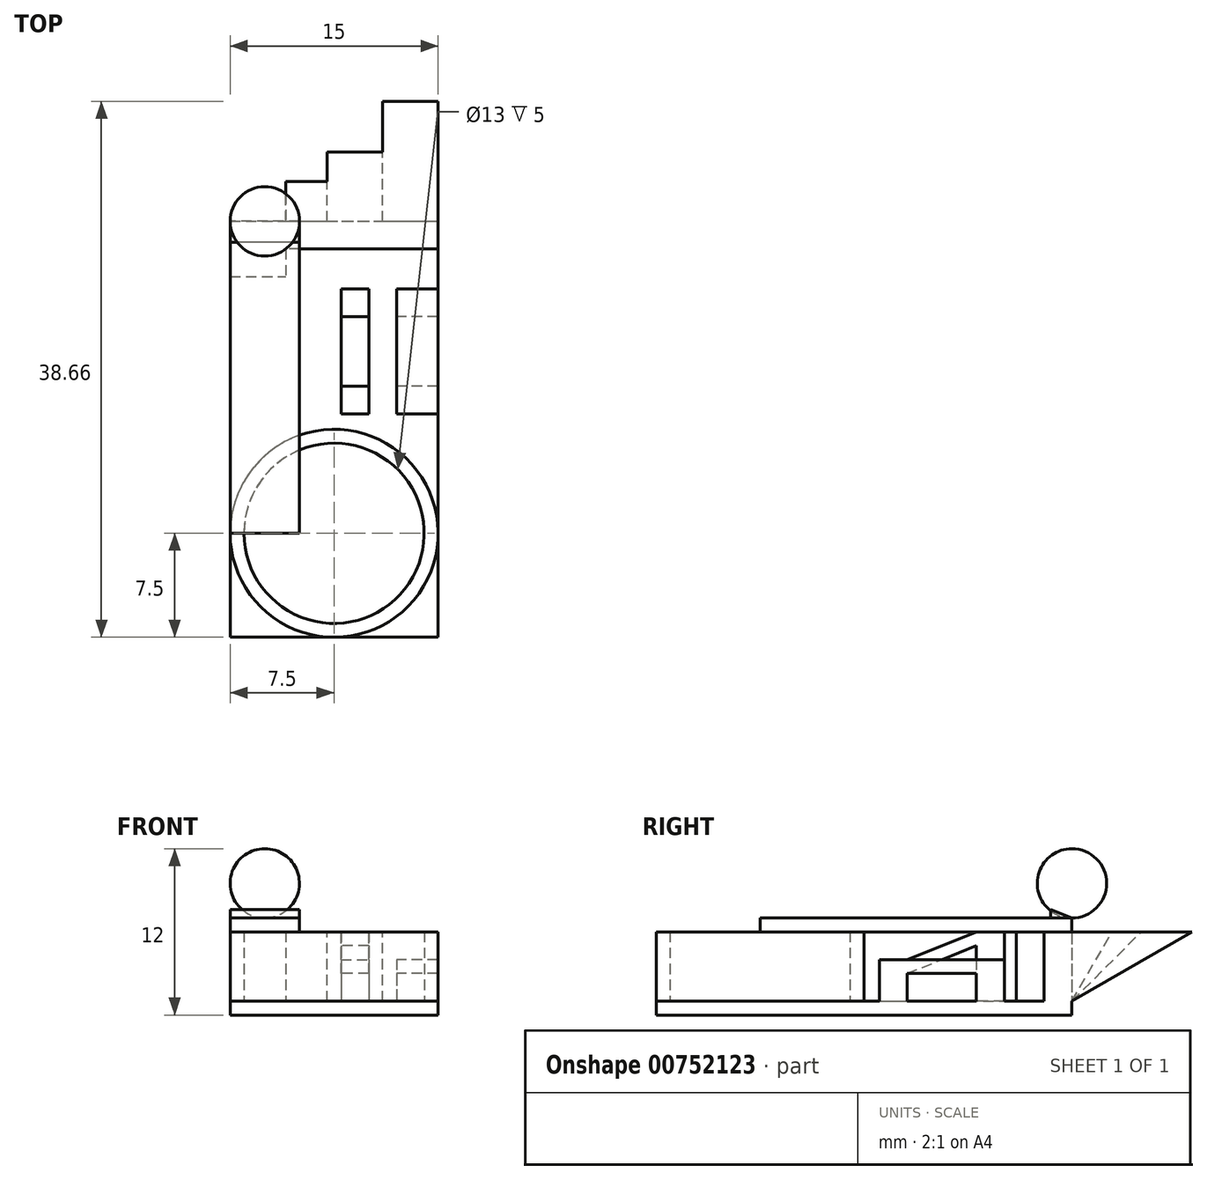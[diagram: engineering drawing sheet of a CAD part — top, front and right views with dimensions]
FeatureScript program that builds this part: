
annotation { "Feature Type Name" : "Feature", "Feature Type Description" : "" }
export const myFeature = defineFeature(function(context is Context, id is Id, definition is map)
    precondition{}
    {
        {
            var Q0;
            Q0=qCreatedBy(makeId("Top.planeOp"),FACE);
            var sketch = newSketch(context, id + "F0", { "sketchPlane" : qUnion([Q0])});
            skLineSegment(sketch, "E0.bottom", {"start": v(0, 0) * mm, "end": v(15, 0) * mm});
            skLineSegment(sketch, "E0.top", {"start": v(0, 30) * mm, "end": v(15, 30) * mm});
            skLineSegment(sketch, "E0.left", {"start": v(0, 0) * mm, "end": v(0, 30) * mm});
            skLineSegment(sketch, "E0.right", {"start": v(15, 0) * mm, "end": v(15, 30) * mm});
            skSolve(sketch);
        }
        {
            var Q0;
            Q0=makeQuery(id+"F0.imprint","IMPRINT",FACE,{"disambiguationData":[TD([[makeQuery(id+"F0.imprint","IMPRINT",EDGE,{"derivedFrom":sQuery(id+"F0.wireOp",EDGE,"E0.bottom")}),1.0]])]});
            extrude(context, id + "F1", {"entities" : qUnion([Q0]), "depth" : 1 * mm, "offsetDistance" : 25 * mm});
        }
        {
            var Q0;
            Q0=makeQuery(id+"F1.opExtrude","CAP_FACE",FACE,{"disambiguationData":[OSD([sQuery(id+"F0.wireOp",EDGE,"E0.bottom"),sQuery(id+"F0.wireOp",EDGE,"E0.top"),sQuery(id+"F0.wireOp",EDGE,"E0.left"),sQuery(id+"F0.wireOp",EDGE,"E0.right")])],"isStart":false});
            var sketch = newSketch(context, id + "F2", { "sketchPlane" : qUnion([Q0])});
            skCircle(sketch, "E1", {"center": v(7.5, 7.5) * mm, "radius": 7.5 * mm});
            skCircle(sketch, "E2", {"center": v(7.5, 7.5) * mm, "radius": 6.5 * mm});
            skSolve(sketch);
        }
        {
            var Q0;
            Q0 = qSketchRegion(id + "F2", true);
            extrude(context, id + "F3", {"entities" : qUnion([Q0]), "operationType" : NewBodyOperationType.ADD, "depth" : 5 * mm, "offsetDistance" : 25 * mm});
        }
        {
            var Q0;
            {var subQ0=sQuery(id+"F0.wireOp",EDGE,"E0.right");var subQ1=sQuery(id+"F0.wireOp",EDGE,"E0.left");var subQ2=sQuery(id+"F0.wireOp",EDGE,"E0.top");var subQ3=makeQuery(id+"F1.opExtrude","CAP_FACE",FACE,{"disambiguationData":[OSD([sQuery(id+"F0.wireOp",EDGE,"E0.bottom"),subQ2,subQ1,subQ0])],"isStart":false});Q0=makeQuery(id+"F3.boolean.opBoolean","SPLIT",FACE,{"disambiguationData":[TD([subQ3,makeQuery(id+"F1.opExtrude","SWEPT_FACE",FACE,{"disambiguationData":[OSD([subQ2])]}),makeQuery(id+"F1.opExtrude","SWEPT_FACE",FACE,{"disambiguationData":[OSD([subQ1])]}),makeQuery(id+"F1.opExtrude","SWEPT_FACE",FACE,{"disambiguationData":[OSD([subQ0])]}),makeQuery(id+"F3.opExtrude","SWEPT_FACE",FACE,{"disambiguationData":[OSD([sQuery(id+"F2.wireOp",EDGE,"E1")])]})])],"derivedFrom":subQ3});}
            var sketch = newSketch(context, id + "F4", { "sketchPlane" : qUnion([Q0])});
            skLineSegment(sketch, "E3.bottom", {"start": v(0, 30) * mm, "end": v(4, 30) * mm});
            skLineSegment(sketch, "E3.top", {"start": v(0, 26) * mm, "end": v(4, 26) * mm});
            skLineSegment(sketch, "E3.left", {"start": v(0, 30) * mm, "end": v(0, 26) * mm});
            skLineSegment(sketch, "E3.right", {"start": v(4, 30) * mm, "end": v(4, 26) * mm});
            skSolve(sketch);
        }
        {
            var Q0;
            Q0 = qSketchRegion(id + "F4", true);
            extrude(context, id + "F5", {"entities" : qUnion([Q0]), "operationType" : NewBodyOperationType.ADD, "depth" : 5 * mm, "offsetDistance" : 25 * mm});
        }
        {
            var Q0;
            Q0=makeQuery(id+"F5.opExtrude","CAP_FACE",FACE,{"disambiguationData":[OSD([sQuery(id+"F4.wireOp",EDGE,"E3.bottom"),sQuery(id+"F4.wireOp",EDGE,"E3.top"),sQuery(id+"F4.wireOp",EDGE,"E3.left"),sQuery(id+"F4.wireOp",EDGE,"E3.right")])],"isStart":false});
            var sketch = newSketch(context, id + "F6", { "sketchPlane" : qUnion([Q0])});
            skLineSegment(sketch, "E4.bottom", {"start": v(0, 30) * mm, "end": v(5, 30) * mm});
            skLineSegment(sketch, "E4.top", {"start": v(0, 7.5) * mm, "end": v(5, 7.5) * mm});
            skLineSegment(sketch, "E4.left", {"start": v(0, 30) * mm, "end": v(0, 7.5) * mm});
            skLineSegment(sketch, "E4.right", {"start": v(5, 30) * mm, "end": v(5, 7.5) * mm});
            skSolve(sketch);
        }
        {
            var Q0;
            Q0 = qSketchRegion(id + "F6", true);
            extrude(context, id + "F7", {"entities" : qUnion([Q0]), "operationType" : NewBodyOperationType.ADD, "depth" : 1 * mm, "offsetDistance" : 25 * mm});
        }
        {
            var Q0;
            Q0=makeQuery(id+"F5.opExtrude","SWEPT_FACE",FACE,{"disambiguationData":[OSD([sQuery(id+"F4.wireOp",EDGE,"E3.right")])]});
            var sketch = newSketch(context, id + "F8", { "sketchPlane" : qUnion([Q0])});
            skLineSegment(sketch, "E5", {"start": v(30, 1) * mm, "end": v(32.89, 6) * mm});
            skLineSegment(sketch, "E6", {"start": v(32.89, 6) * mm, "end": v(30, 6) * mm});
            skLineSegment(sketch, "E7", {"start": v(30, 6) * mm, "end": v(28, 6) * mm});
            skLineSegment(sketch, "E8", {"start": v(28, 6) * mm, "end": v(28, 1) * mm});
            skLineSegment(sketch, "E9", {"start": v(28, 1) * mm, "end": v(30, 1) * mm});
            skSolve(sketch);
        }
        {
            var Q0;
            Q0 = qSketchRegion(id + "F8", true);
            extrude(context, id + "F9", {"entities" : qUnion([Q0]), "operationType" : NewBodyOperationType.ADD, "depth" : 3 * mm, "offsetDistance" : 25 * mm});
        }
        {
            var Q0;
            Q0=makeQuery(id+"F9.opExtrude","CAP_FACE",FACE,{"disambiguationData":[OSD([sQuery(id+"F8.wireOp",EDGE,"E5"),sQuery(id+"F8.wireOp",EDGE,"E6"),sQuery(id+"F8.wireOp",EDGE,"E7"),sQuery(id+"F8.wireOp",EDGE,"E8"),sQuery(id+"F8.wireOp",EDGE,"E9")])],"isStart":false});
            var sketch = newSketch(context, id + "F10", { "sketchPlane" : qUnion([Q0])});
            skLineSegment(sketch, "E10", {"start": v(28, 1) * mm, "end": v(30, 1) * mm});
            skLineSegment(sketch, "E11", {"start": v(30, 1) * mm, "end": v(35, 6) * mm});
            skLineSegment(sketch, "E12", {"start": v(35, 6) * mm, "end": v(30, 6) * mm});
            skLineSegment(sketch, "E13", {"start": v(30, 6) * mm, "end": v(28, 6) * mm});
            skLineSegment(sketch, "E14", {"start": v(28, 6) * mm, "end": v(28, 1) * mm});
            skLineSegment(sketch, "E15", {"start": v(30, 1) * mm, "end": v(30, 6) * mm, "construction": true});
            skSolve(sketch);
        }
        {
            var Q0;
            Q0 = qSketchRegion(id + "F10", true);
            extrude(context, id + "F11", {"entities" : qUnion([Q0]), "operationType" : NewBodyOperationType.ADD, "depth" : 4 * mm, "offsetDistance" : 25 * mm});
        }
        {
            var Q0;
            Q0=makeQuery(id+"F11.opExtrude","CAP_FACE",FACE,{"disambiguationData":[OSD([sQuery(id+"F10.wireOp",EDGE,"E10"),sQuery(id+"F10.wireOp",EDGE,"E11"),sQuery(id+"F10.wireOp",EDGE,"E12"),sQuery(id+"F10.wireOp",EDGE,"E13"),sQuery(id+"F10.wireOp",EDGE,"E14")])],"isStart":false});
            var sketch = newSketch(context, id + "F12", { "sketchPlane" : qUnion([Q0])});
            skLineSegment(sketch, "E16", {"start": v(28, 1) * mm, "end": v(30, 1) * mm});
            skLineSegment(sketch, "E17", {"start": v(30, 1) * mm, "end": v(38.66, 6) * mm});
            skLineSegment(sketch, "E18", {"start": v(38.66, 6) * mm, "end": v(30, 6) * mm});
            skLineSegment(sketch, "E19", {"start": v(30, 6) * mm, "end": v(28, 6) * mm});
            skLineSegment(sketch, "E20", {"start": v(28, 6) * mm, "end": v(28, 1) * mm});
            skLineSegment(sketch, "E21", {"start": v(30, 1) * mm, "end": v(30, 6) * mm, "construction": true});
            skSolve(sketch);
        }
        {
            var Q0;
            Q0 = qSketchRegion(id + "F12", true);
            extrude(context, id + "F13", {"entities" : qUnion([Q0]), "operationType" : NewBodyOperationType.ADD, "depth" : 4 * mm, "offsetDistance" : 25 * mm});
        }
        {
            var Q0;
            {var subQ0=sQuery(id+"F0.wireOp",EDGE,"E0.right");var subQ1=sQuery(id+"F0.wireOp",EDGE,"E0.left");var subQ2=sQuery(id+"F0.wireOp",EDGE,"E0.top");var subQ3=makeQuery(id+"F1.opExtrude","CAP_FACE",FACE,{"disambiguationData":[OSD([sQuery(id+"F0.wireOp",EDGE,"E0.bottom"),subQ2,subQ1,subQ0])],"isStart":false});Q0=makeQuery(id+"F3.boolean.opBoolean","SPLIT",FACE,{"disambiguationData":[TD([subQ3,makeQuery(id+"F1.opExtrude","SWEPT_FACE",FACE,{"disambiguationData":[OSD([subQ2])]}),makeQuery(id+"F1.opExtrude","SWEPT_FACE",FACE,{"disambiguationData":[OSD([subQ1])]}),makeQuery(id+"F1.opExtrude","SWEPT_FACE",FACE,{"disambiguationData":[OSD([subQ0])]}),makeQuery(id+"F3.opExtrude","SWEPT_FACE",FACE,{"disambiguationData":[OSD([sQuery(id+"F2.wireOp",EDGE,"E1")])]})])],"derivedFrom":subQ3});}
            var sketch = newSketch(context, id + "F14", { "sketchPlane" : qUnion([Q0])});
            skLineSegment(sketch, "E22.bottom", {"start": v(15, 16.11) * mm, "end": v(12, 16.11) * mm});
            skLineSegment(sketch, "E22.top", {"start": v(15, 18.11) * mm, "end": v(12, 18.11) * mm});
            skLineSegment(sketch, "E22.left", {"start": v(15, 16.11) * mm, "end": v(15, 18.11) * mm});
            skLineSegment(sketch, "E22.right", {"start": v(12, 16.11) * mm, "end": v(12, 18.11) * mm});
            skLineSegment(sketch, "E23.bottom", {"start": v(15, 23.11) * mm, "end": v(12, 23.11) * mm});
            skLineSegment(sketch, "E23.top", {"start": v(15, 25.11) * mm, "end": v(12, 25.11) * mm});
            skLineSegment(sketch, "E23.left", {"start": v(15, 23.11) * mm, "end": v(15, 25.11) * mm});
            skLineSegment(sketch, "E23.right", {"start": v(12, 23.11) * mm, "end": v(12, 25.11) * mm});
            skSolve(sketch);
        }
        {
            var Q0;
            Q0 = qSketchRegion(id + "F14", true);
            extrude(context, id + "F15", {"entities" : qUnion([Q0]), "operationType" : NewBodyOperationType.ADD, "depth" : 2 * mm, "offsetDistance" : 25 * mm});
        }
        {
            var Q0;
            Q0=makeQuery(id+"F15.opExtrude","CAP_FACE",FACE,{"disambiguationData":[OSD([sQuery(id+"F14.wireOp",EDGE,"E22.bottom"),sQuery(id+"F14.wireOp",EDGE,"E22.top"),sQuery(id+"F14.wireOp",EDGE,"E22.left"),sQuery(id+"F14.wireOp",EDGE,"E22.right")])],"isStart":false});
            var sketch = newSketch(context, id + "F16", { "sketchPlane" : qUnion([Q0])});
            skLineSegment(sketch, "E24.bottom", {"start": v(12, 16.11) * mm, "end": v(15, 16.11) * mm});
            skLineSegment(sketch, "E24.top", {"start": v(12, 25.11) * mm, "end": v(15, 25.11) * mm});
            skLineSegment(sketch, "E24.left", {"start": v(12, 16.11) * mm, "end": v(12, 25.11) * mm});
            skLineSegment(sketch, "E24.right", {"start": v(15, 16.11) * mm, "end": v(15, 25.11) * mm});
            skSolve(sketch);
        }
        {
            var Q0;
            Q0 = qSketchRegion(id + "F16", true);
            extrude(context, id + "F17", {"entities" : qUnion([Q0]), "operationType" : NewBodyOperationType.ADD, "depth" : 1 * mm, "offsetDistance" : 25 * mm});
        }
        {
            var Q0;
            {var subQ12=sQuery(id+"F14.wireOp",EDGE,"E22.bottom");Q0=makeQuery(id+"F14.imprint","IMPRINT",FACE,{"disambiguationData":[TD([[makeQuery(id+"F14.imprint","IMPRINT",EDGE,{"derivedFrom":subQ12}),1.0]])]});}
            var sketch = newSketch(context, id + "F18", { "sketchPlane" : qUnion([Q0])});
            skLineSegment(sketch, "E25.bottom", {"start": v(10, 16.11) * mm, "end": v(8, 16.11) * mm});
            skLineSegment(sketch, "E25.top", {"start": v(10, 18.11) * mm, "end": v(8, 18.11) * mm});
            skLineSegment(sketch, "E25.left", {"start": v(10, 16.11) * mm, "end": v(10, 18.11) * mm});
            skLineSegment(sketch, "E25.right", {"start": v(8, 16.11) * mm, "end": v(8, 18.11) * mm});
            skLineSegment(sketch, "E26", {"start": v(12, 16.11) * mm, "end": v(10, 16.11) * mm, "construction": true});
            skLineSegment(sketch, "E27.bottom", {"start": v(10, 25.11) * mm, "end": v(8, 25.11) * mm});
            skLineSegment(sketch, "E27.top", {"start": v(10, 23.11) * mm, "end": v(8, 23.11) * mm});
            skLineSegment(sketch, "E27.left", {"start": v(10, 25.11) * mm, "end": v(10, 23.11) * mm});
            skLineSegment(sketch, "E27.right", {"start": v(8, 25.11) * mm, "end": v(8, 23.11) * mm});
            skLineSegment(sketch, "E28", {"start": v(8, 23.11) * mm, "end": v(8, 18.11) * mm, "construction": true});
            skLineSegment(sketch, "E29", {"start": v(12, 25.11) * mm, "end": v(10, 25.11) * mm, "construction": true});
            skSolve(sketch);
        }
        {
            var Q0;
            Q0=makeQuery(id+"F18.imprint","IMPRINT",FACE,{"disambiguationData":[TD([[makeQuery(id+"F18.imprint","IMPRINT",EDGE,{"derivedFrom":sQuery(id+"F18.wireOp",EDGE,"E25.bottom")}),-1.0]])]});
            extrude(context, id + "F19", {"entities" : qUnion([Q0]), "operationType" : NewBodyOperationType.ADD, "depth" : 2 * mm, "offsetDistance" : 25 * mm});
        }
        {
            var Q0;
            Q0=makeQuery(id+"F18.imprint","IMPRINT",FACE,{"disambiguationData":[TD([[makeQuery(id+"F18.imprint","IMPRINT",EDGE,{"derivedFrom":sQuery(id+"F18.wireOp",EDGE,"E27.bottom")}),1.0]])]});
            extrude(context, id + "F20", {"entities" : qUnion([Q0]), "operationType" : NewBodyOperationType.ADD, "depth" : 4 * mm, "offsetDistance" : 25 * mm});
        }
        {
            var Q0;
            Q0=makeQuery(id+"F19.opExtrude","SWEPT_FACE",FACE,{"disambiguationData":[OSD([sQuery(id+"F18.wireOp",EDGE,"E25.left")])]});
            var sketch = newSketch(context, id + "F21", { "sketchPlane" : qUnion([Q0])});
            skLineSegment(sketch, "E30", {"start": v(18.11, 3) * mm, "end": v(23.11, 5) * mm});
            skLineSegment(sketch, "E31", {"start": v(18.11, 3) * mm, "end": v(16.11, 3) * mm});
            skLineSegment(sketch, "E32", {"start": v(16.11, 3) * mm, "end": v(16.11, 4) * mm});
            skLineSegment(sketch, "E33", {"start": v(16.11, 4) * mm, "end": v(18.11, 4) * mm});
            skLineSegment(sketch, "E34", {"start": v(18.11, 4) * mm, "end": v(23.11, 6) * mm});
            skLineSegment(sketch, "E35", {"start": v(23.11, 6) * mm, "end": v(25.11, 6) * mm});
            skLineSegment(sketch, "E36", {"start": v(25.11, 6) * mm, "end": v(25.11, 5) * mm});
            skLineSegment(sketch, "E37", {"start": v(25.11, 5) * mm, "end": v(23.11, 5) * mm});
            skSolve(sketch);
        }
        {
            var Q0;
            Q0 = qSketchRegion(id + "F21", true);
            extrude(context, id + "F22", {"entities" : qUnion([Q0]), "operationType" : NewBodyOperationType.ADD, "oppositeDirection" : true, "depth" : 2 * mm, "offsetDistance" : 25 * mm});
        }
        {
            var Q0;
            Q0=makeQuery(id+"F7.opExtrude","CAP_EDGE",EDGE,{"disambiguationData":[OSD([sQuery(id+"F6.wireOp",EDGE,"E4.bottom")])],"isStart":false});
            cPoint(context, id + "F23", {"entities" : qUnion([Q0]), "parameter" : 0.5});
        }
        {
            var Q0;
            Q0 = qCreatedBy(id + "F23" ,VERTEX);
            var Q1;
            Q1=makeQuery(id+"F7.opExtrude","CAP_EDGE",EDGE,{"disambiguationData":[OSD([sQuery(id+"F6.wireOp",EDGE,"E4.bottom")])],"isStart":false});
            cPlane(context, id + "F24", {"entities" : qUnion([Q0, Q1]), "cplaneType" : CPlaneType.CURVE_POINT, "offset" : 25 * mm, "width" : 150 * mm, "height" : 150 * mm});
        }
        {
            var Q0;
            Q0=qCreatedBy(id+"F24.planeOp",FACE);
            var sketch = newSketch(context, id + "F25", { "sketchPlane" : qUnion([Q0])});
            skLineSegment(sketch, "E38", {"start": v(30, 7) * mm, "end": v(30, 9.5) * mm, "construction": true});
            skLineSegment(sketch, "E39", {"start": v(30, 9.5) * mm, "end": v(30, 12) * mm, "construction": true});
            skPoint(sketch, "E40", {"position": v(30, 12) * mm});
            skArc(sketch, "E41", {"start": v(30, 7) * mm, "mid": v(32.5, 9.5) * mm, "end": v(30, 12) * mm});
            skLineSegment(sketch, "E42", {"start": v(30, 12) * mm, "end": v(30, 7) * mm});
            skSolve(sketch);
        }
        {
            var Q0;
            Q0=makeQuery(id+"F25.imprint","IMPRINT",FACE,{"disambiguationData":[TD([[makeQuery(id+"F25.imprint","IMPRINT",EDGE,{"derivedFrom":sQuery(id+"F25.wireOp",EDGE,"E41")}),1.0]])]});
            var Q1;
            Q1=sQuery(id+"F25.wireOp",EDGE,"E42");
            revolve(context, id + "F26", {"surfaceOperationType" : NewSurfaceOperationType.NEW, "entities" : qUnion([Q0]), "axis" : qUnion([Q1]), "revolveType" : RevolveType.FULL});
        }
        {
            var Q0;
            Q0=makeQuery(id+"F7.boolean.opBoolean","MERGE",FACE,{"derivedFrom":[makeQuery(id+"F5.boolean.opBoolean","MERGE",FACE,{"derivedFrom":[makeQuery(id+"F1.opExtrude","SWEPT_FACE",FACE,{"disambiguationData":[OSD([sQuery(id+"F0.wireOp",EDGE,"E0.left")])]}),makeQuery(id+"F5.opExtrude","SWEPT_FACE",FACE,{"disambiguationData":[OSD([sQuery(id+"F4.wireOp",EDGE,"E3.left")])]})]}),makeQuery(id+"F7.opExtrude","SWEPT_FACE",FACE,{"disambiguationData":[OSD([sQuery(id+"F6.wireOp",EDGE,"E4.left")])]})]});
            var sketch = newSketch(context, id + "F27", { "sketchPlane" : qUnion([Q0])});
            skLineSegment(sketch, "E43", {"start": v(-30, 7) * mm, "end": v(-28.48, 7) * mm});
            skLineSegment(sketch, "E44", {"start": v(-28.48, 7) * mm, "end": v(-28.48, 7.6) * mm});
            skLineSegment(sketch, "E45", {"start": v(-28.48, 7.6) * mm, "end": v(-30, 7) * mm});
            skSolve(sketch);
        }
        {
            var Q0;
            Q0 = qSketchRegion(id + "F27", true);
            extrude(context, id + "F28", {"entities" : qUnion([Q0]), "oppositeDirection" : true, "depth" : 5 * mm, "offsetDistance" : 25 * mm});
        }
    });
